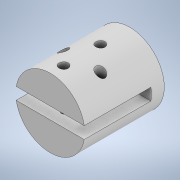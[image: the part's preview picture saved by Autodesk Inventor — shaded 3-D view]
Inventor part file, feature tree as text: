
AUTODESK INVENTOR PART (.ipt)
format: ipt  version: 2022 (Build 260153000, 153)  size: 183,296 bytes
history: native  units: mm
features: extrude x5, sketch x5, plane x2
ambient origin geometry x8: Origin, YZ Plane, XZ Plane, XY Plane, X Axis, Y Axis, Z Axis, Center Point
bodies: Solid1 (feature_tree)
feature tree (12):
  extrude  "Extrusion1"  Depth=3.25mm
  extrude  "Extrusion2"  Depth=31.2mm TaperAngle=0.0deg
  plane  "Work Plane1"
  sketch  "Sketch3"  dims[d8=2.5mm d10=40.0mm d12=360.0deg]
  plane  "Work Plane2"
  extrude  "Extrusion3"  Depth=2.5mm TaperAngle=360.0deg
  sketch  "Sketch4"  dims[d14=31.2mm d15=0.0mm d16=5.0mm]
  extrude  "Extrusion4"  Depth=5.0mm
  extrude  "Extrusion5"  Depth=5.0mm TaperAngle=0.0deg
  sketch  "Sketch1"  dims[d1=7.0mm d2=0.0mm d3=3.25mm]
  sketch  "Sketch2"  dims[d4=3.25mm d5=31.2mm d6=0.0mm]
  sketch  "Sketch5"  dims[d17=5.0mm d18=5.0mm d19=0.0mm d20=8.0mm d21=0.0mm]
